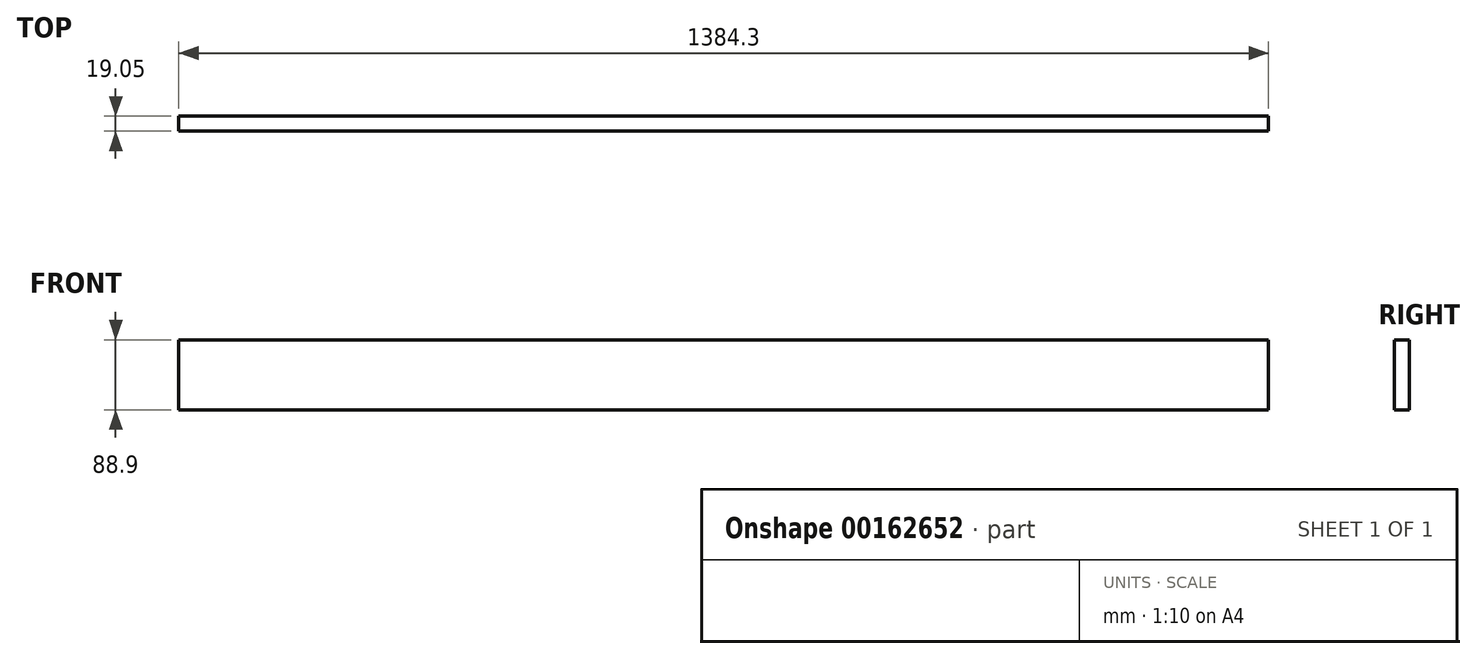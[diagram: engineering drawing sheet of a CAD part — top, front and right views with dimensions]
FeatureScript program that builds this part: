
annotation { "Feature Type Name" : "Feature", "Feature Type Description" : "" }
export const myFeature = defineFeature(function(context is Context, id is Id, definition is map)
    precondition{}
    {
        {
            var Q0;
            Q0=qCreatedBy(makeId("Front.planeOp"),FACE);
            var sketch = newSketch(context, id + "F0", { "sketchPlane" : qUnion([Q0])});
            skLineSegment(sketch, "E0.bottom", {"start": v(-686.4, 61.77) * mm, "end": v(697.9, 61.77) * mm});
            skLineSegment(sketch, "E0.top", {"start": v(-686.4, -27.13) * mm, "end": v(697.9, -27.13) * mm});
            skLineSegment(sketch, "E0.left", {"start": v(-686.4, 61.77) * mm, "end": v(-686.4, -27.13) * mm});
            skLineSegment(sketch, "E0.right", {"start": v(697.9, 61.77) * mm, "end": v(697.9, -27.13) * mm});
            skSolve(sketch);
        }
        {
            var Q0;
            Q0 = qSketchRegion(id + "F0", true);
            extrude(context, id + "F1", {"entities" : qUnion([Q0]), "depth" : 19.05 * mm});
        }
    });
